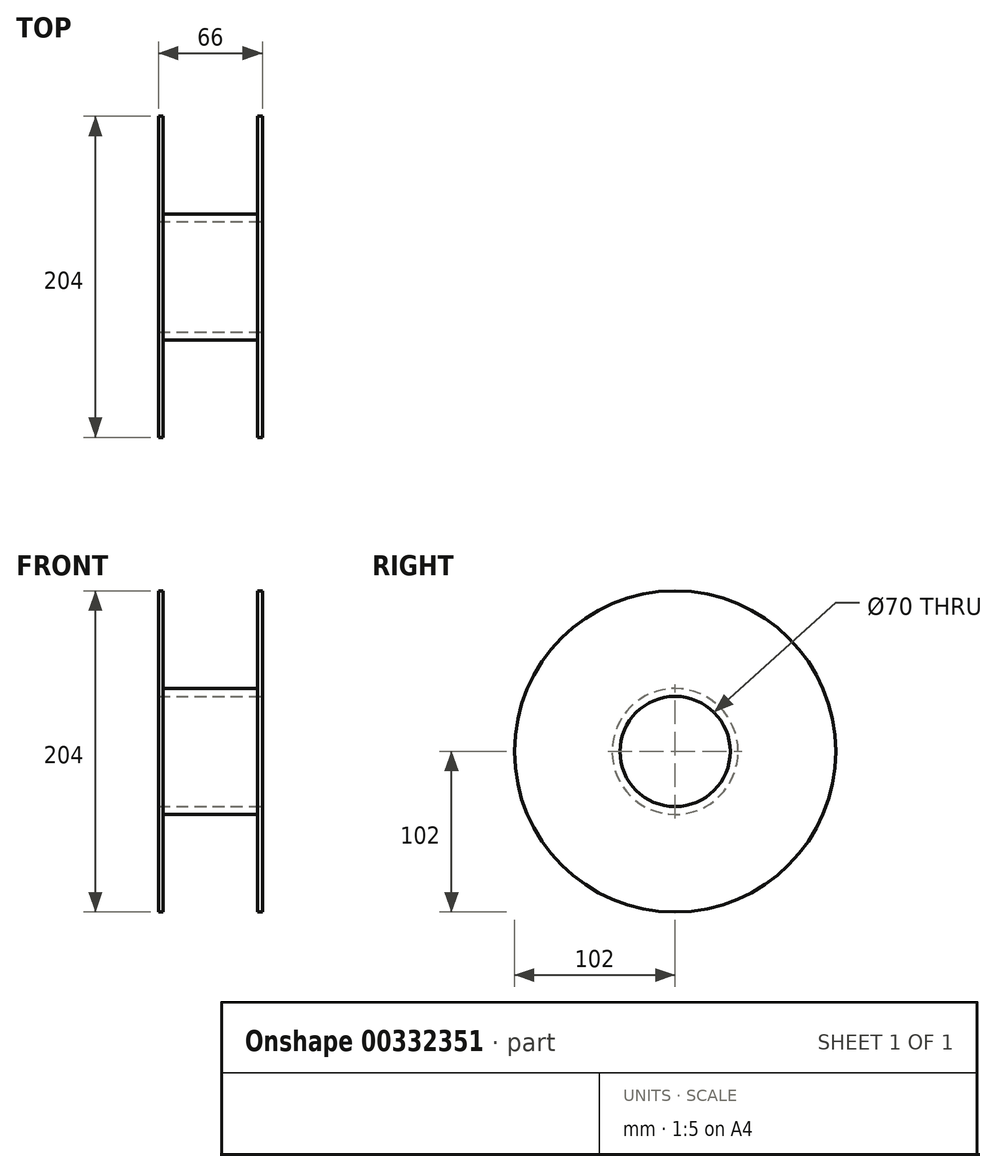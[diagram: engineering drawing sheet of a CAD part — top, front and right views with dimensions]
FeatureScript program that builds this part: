
annotation { "Feature Type Name" : "Feature", "Feature Type Description" : "" }
export const myFeature = defineFeature(function(context is Context, id is Id, definition is map)
    precondition{}
    {
        {
            var Q0;
            Q0=qCreatedBy(makeId("Front.planeOp"),FACE);
            var sketch = newSketch(context, id + "F0", { "sketchPlane" : qUnion([Q0])});
            skLineSegment(sketch, "E0", {"start": v(0, 40) * mm, "end": v(-30, 40) * mm});
            skLineSegment(sketch, "E1", {"start": v(-30, 40) * mm, "end": v(-30, 102) * mm});
            skLineSegment(sketch, "E2", {"start": v(-30, 102) * mm, "end": v(-33, 102) * mm});
            skLineSegment(sketch, "E3", {"start": v(-33, 102) * mm, "end": v(-33, 35) * mm});
            skLineSegment(sketch, "E4.MirrorCS", {"start": v(30, 102) * mm, "end": v(33, 102) * mm});
            skLineSegment(sketch, "E5.MirrorCS", {"start": v(30, 40) * mm, "end": v(30, 102) * mm});
            skLineSegment(sketch, "E6.MirrorCS", {"start": v(0, 40) * mm, "end": v(30, 40) * mm});
            skLineSegment(sketch, "E7.MirrorCS", {"start": v(33, 102) * mm, "end": v(33, 35) * mm});
            skLineSegment(sketch, "E8", {"start": v(-33, 35) * mm, "end": v(33, 35) * mm});
            skLineSegment(sketch, "E9", {"start": v(0, 0) * mm, "end": v(-4.65, 0) * mm});
            skSolve(sketch);
        }
        {
            var Q0;
            Q0=makeQuery(id+"F0.imprint","IMPRINT",FACE,{"disambiguationData":[TD([[makeQuery(id+"F0.imprint","IMPRINT",EDGE,{"derivedFrom":sQuery(id+"F0.wireOp",EDGE,"E0")}),1.0]])]});
            var Q1;
            Q1=sQuery(id+"F0.wireOp",EDGE,"E9");
            revolve(context, id + "F1", {"entities" : qUnion([Q0]), "axis" : qUnion([Q1]), "revolveType" : RevolveType.FULL});
        }
    });
